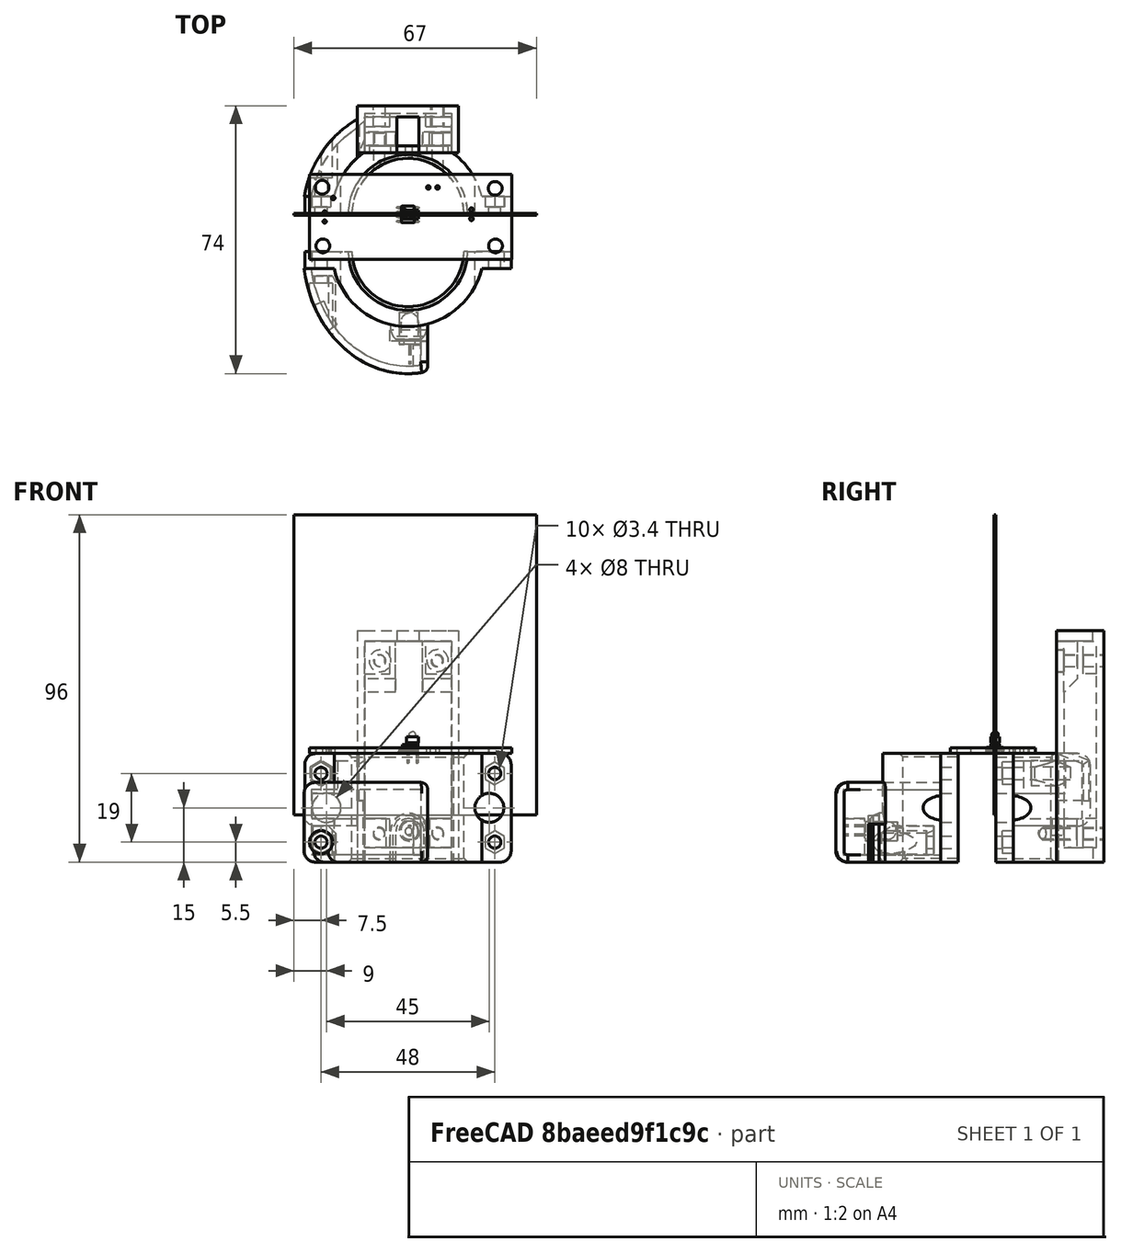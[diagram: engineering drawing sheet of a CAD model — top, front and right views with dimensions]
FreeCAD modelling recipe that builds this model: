
FCSTD DOCUMENT  (FreeCAD 0.21R33668 +26 (Git))
Label: Senzor
License: All rights reserved
LicenseURL: http://en.wikipedia.org/wiki/All_rights_reserved
objects: Part::Box×33, Part::Cut×27, Part::Cylinder×24, Part::MultiFuse×22, App::Part×20, Part::Feature×19, Part::Chamfer×17, Part::Prism×5, Part::Fillet×5, Part::FeaturePython×4, Part::Part2DObjectPython×4, Part::Extrusion×4, Part::MultiCommon×2, Part::Thickness×2, Part::Wedge×1, Spreadsheet::Sheet×1, App::DocumentObjectGroup×1
note: 169 computed .brp shape members not serialized (recipe doc carries the construction recipe); baked Part::Feature solids carry a one-line shape summary decoded from their .brp

FEATURE [Part::Box] Box022  label="Cube022"
  AttacherType = Attacher::AttachEngine3D
  Height = 4
  Length = 24
  Placement = pos=(-12,16,26) rot=(0,0,1;0rad)
  Width = 11
FEATURE [Part::Cylinder] Cylinder017
  Angle = 360
  AttacherType = Attacher::AttachEngine3D
  FirstAngle = 0
  Height = 30
  Radius = 15.5
  SecondAngle = 0
FEATURE [Part::Cylinder] Cylinder018
  Angle = 360
  AttacherType = Attacher::AttachEngine3D
  FirstAngle = 0
  Height = 30
  Radius = 21
  SecondAngle = 0
FEATURE [Part::Box] Box024  label="Cube024"
  AttacherType = Attacher::AttachEngine3D
  Height = 8
  Length = 24
  Placement = pos=(-12,15.5,18) rot=(0,0,1;0rad)
  Width = 7
FEATURE [Part::Box] Box025  label="Cube025"
  AttacherType = Attacher::AttachEngine3D
  Height = 8
  Length = 24
  Placement = pos=(12,27,18) rot=(0,0,1;3.14159rad)
  Width = 2.5
FEATURE [Part::Cut] Cut026
  Base = -> Cylinder018
  Tool = -> Cylinder017
FEATURE [Part::Box] Box027  label="Cube027"
  AttacherType = Attacher::AttachEngine3D
  Height = 35
  Length = 29
  Placement = pos=(-14,18,-17) rot=(0,0,1;0rad)
  Width = 11
FEATURE [Part::Cut] Cut027
  Base = -> Cut026
  Tool = -> Box027
FEATURE [Part::Box] Box028  label="Cube028"
  AttacherType = Attacher::AttachEngine3D
  Height = 20
  Length = 12
  Placement = pos=(-6,19,6) rot=(0,0,1;0rad)
  Width = 5
FEATURE [Part::MultiFuse] Fusion015
  Shapes = -> [Cut027,Box024]
FEATURE [Part::Cut] Cut028
  Base = -> Fusion015
  Tool = -> Box028
FEATURE [Part::Cylinder] Cylinder023
  Angle = 360
  AttacherType = Attacher::AttachEngine3D
  FirstAngle = 0
  Height = 44
  Placement = pos=(-0.2,19.5,21.5) rot=(1,0,0;1.5708rad)
  Radius = 1
  SecondAngle = 0
FEATURE [Part::Cylinder] Cylinder024
  Angle = 360
  AttacherType = Attacher::AttachEngine3D
  FirstAngle = 0
  Height = 5
  Placement = pos=(-0.2,-17,21.5) rot=(1,0,0;1.5708rad)
  Radius = 2.6
  SecondAngle = 0
FEATURE [Part::Cylinder] Cylinder025
  Angle = 360
  AttacherType = Attacher::AttachEngine3D
  FirstAngle = 0
  Height = 22
  Placement = pos=(0,0,-3) rot=(0,0,1;0rad)
  Radius = 1.7
  SecondAngle = 0
FEATURE [Part::Prism] Prism003
  AttacherType = Attacher::AttachEngine3D
  Circumradius = 3.1
  FirstAngle = 0
  Height = 4
  Polygon = 6
  SecondAngle = 0
FEATURE [Part::MultiFuse] Fusion017
  Placement = pos=(24,6,5.5) rot=(0.935113,-0.250563,0.250563;1.63783rad)
  Shapes = -> [Cylinder025,Prism003]
FEATURE [Part::Box] Box031  label="Cube031"
  AttacherType = Attacher::AttachEngine3D
  Height = 19
  Length = 7.5
  Placement = pos=(-4,18,-31.5) rot=(0,0,1;0rad)
  Width = 10
FEATURE [Part::Box] Box032  label="Cube032"
  AttacherType = Attacher::AttachEngine3D
  Height = 83
  Length = 67
  Placement = pos=(-31.5,-0.25,-17) rot=(0,0,1;0rad)
  Width = 0.5
FEATURE [Part::Box] Box033  label="Cube033"
  AttacherType = Attacher::AttachEngine3D
  Height = 30
  Length = 11
  Placement = pos=(17.5,-5,0) rot=(0,0,1;0rad)
  Width = 10
FEATURE [Part::Cylinder] Cylinder032
  Angle = 360
  AttacherType = Attacher::AttachEngine3D
  FirstAngle = 0
  Height = 22
  Placement = pos=(0,0,-3) rot=(0,0,1;0rad)
  Radius = 1.7
  SecondAngle = 0
FEATURE [Part::Cylinder] Cylinder034
  Angle = 360
  AttacherType = Attacher::AttachEngine3D
  FirstAngle = 0
  Height = 32
  Placement = pos=(22.5,13,15) rot=(1,0,0;1.5708rad)
  Radius = 4
  SecondAngle = 0
FEATURE [Part::Prism] Prism006
  AttacherType = Attacher::AttachEngine3D
  Circumradius = 3.1
  FirstAngle = 0
  Height = 4
  Polygon = 6
  SecondAngle = 0
FEATURE [Part::MultiFuse] Fusion021
  Placement = pos=(24,6,24.5) rot=(0.935113,-0.250563,0.250563;1.63783rad)
  Shapes = -> [Cylinder032,Prism006]
FEATURE [Part::Chamfer] Chamfer022
  Base = -> Box022
  Edges = 1 edges r=0.6: [Edge10]
FEATURE [Part::Cylinder] Cylinder030
  Angle = 360
  AttacherType = Attacher::AttachEngine3D
  FirstAngle = 0
  Height = 17
  Placement = pos=(7.7,28,-25.6) rot=(1,0,0;1.5708rad)
  Radius = 1.6
  SecondAngle = 0
FEATURE [Part::Cylinder] Cylinder031
  Angle = 360
  AttacherType = Attacher::AttachEngine3D
  FirstAngle = 0
  Height = 15
  Placement = pos=(-8.2,27,-25.7) rot=(1,0,0;1.5708rad)
  Radius = 1.6
  SecondAngle = 0
FEATURE [Part::Box] Box026  label="Cube026"
  AttacherType = Attacher::AttachEngine3D
  Height = 49
  Length = 24
  Placement = pos=(-12,17,-31) rot=(0,0,1;0rad)
  Width = 2
FEATURE [Part::Box] Box034  label="Cube034"
  AttacherType = Attacher::AttachEngine3D
  Height = 14
  Length = 24
  Placement = pos=(-12,19,-31) rot=(0,0,1;0rad)
  Width = 3.7
FEATURE [Part::Chamfer] Chamfer023
  Base = -> Box034
  Edges = 1 edges r=3.6: [Edge12]
FEATURE [Part::Cut] Cut048
  Base = -> Chamfer023
  Tool = -> Box031
FEATURE [Part::MultiFuse] Fusion025
  Shapes = -> [Cut048,Box026]
FEATURE [Part::MultiFuse] Fusion026
  Shapes = -> [Cylinder030,Cylinder031]
FEATURE [Part::Cut] Cut049
  Base = -> Fusion025
  Tool = -> Fusion026
FEATURE [Part::Cylinder] Cylinder035
  Angle = 360
  AttacherType = Attacher::AttachEngine3D
  FirstAngle = 0
  Height = 17
  Placement = pos=(-8.2,28,22) rot=(1,0,0;1.5708rad)
  Radius = 1.6
  SecondAngle = 0
FEATURE [Part::Cylinder] Cylinder036
  Angle = 360
  AttacherType = Attacher::AttachEngine3D
  FirstAngle = 0
  Height = 17
  Placement = pos=(8,28,22.2) rot=(1,0,0;1.5708rad)
  Radius = 1.6
  SecondAngle = 0
FEATURE [Part::Cut] Cut050
  Base = -> Cut028
  Tool = -> Cylinder023
FEATURE [Part::Cut] Cut051
  Base = -> Cut050
  Tool = -> Cylinder024
FEATURE [Part::MultiFuse] Fusion027
  Shapes = -> [Cylinder036,Cylinder035]
FEATURE [Part::Cylinder] Cylinder037
  Angle = 360
  AttacherType = Attacher::AttachEngine3D
  FirstAngle = 0
  Height = 10
  Placement = pos=(-8.2,19,-25.7) rot=(1,0,0;1.5708rad)
  Radius = 3
  SecondAngle = 0
FEATURE [Part::Cylinder] Cylinder038
  Angle = 360
  AttacherType = Attacher::AttachEngine3D
  FirstAngle = 0
  Height = 10
  Placement = pos=(7.7,19,-25.6) rot=(1,0,0;1.5708rad)
  Radius = 3
  SecondAngle = 0
FEATURE [Part::MultiFuse] Fusion031
  Shapes = -> [Cylinder037,Cylinder038]
FEATURE [Part::Cut] Cut053
  Base = -> Cut049
  Tool = -> Fusion031
FEATURE [Part::Feature] Solid  label="LED_D5.0mm_Clear"
  Placement = pos=(0.5,-38.9,-20) rot=(0.57735,-0.57735,-0.57735;4.18879rad)
  shape: bbox 5.8 x 14.1 x 5.4 mm, 16 faces (baked)
FEATURE [Part::Box] Box035  label="Cube035"
  AttacherType = Attacher::AttachEngine3D
  Height = 10
  Length = 10
  Placement = pos=(-5,21.5,14) rot=(0,0,1;0rad)
  Width = 6.5
FEATURE [Part::Cut] Cut054
  Base = -> Box033
  Tool = -> Fusion021
FEATURE [Part::Cut] Cut055
  Base = -> Cut054
  Tool = -> Fusion017
FEATURE [Part::Cut] Cut056
  Base = -> Box025
  Tool = -> Box035
FEATURE [Part::Box] Box036  label="Cube036"
  AttacherType = Attacher::AttachEngine3D
  Height = 30
  Length = 11
  Placement = pos=(17.5,-5,0) rot=(0,0,1;0rad)
  Width = 10
FEATURE [Part::Cylinder] Cylinder039
  Angle = 360
  AttacherType = Attacher::AttachEngine3D
  FirstAngle = 0
  Height = 22
  Placement = pos=(0,0,-3) rot=(0,0,1;0rad)
  Radius = 1.7
  SecondAngle = 0
FEATURE [Part::Cylinder] Cylinder040
  Angle = 360
  AttacherType = Attacher::AttachEngine3D
  FirstAngle = 0
  Height = 22
  Placement = pos=(0,0,-3) rot=(0,0,1;0rad)
  Radius = 1.7
  SecondAngle = 0
FEATURE [Part::Prism] Prism007
  AttacherType = Attacher::AttachEngine3D
  Circumradius = 3.1
  FirstAngle = 0
  Height = 4
  Polygon = 6
  SecondAngle = 0
FEATURE [Part::MultiFuse] Fusion032
  Placement = pos=(24,6,5.5) rot=(0.935113,-0.250563,0.250563;1.63783rad)
  Shapes = -> [Cylinder039,Prism007]
FEATURE [Part::Prism] Prism008
  AttacherType = Attacher::AttachEngine3D
  Circumradius = 3.1
  FirstAngle = 0
  Height = 4
  Polygon = 6
  SecondAngle = 0
FEATURE [Part::MultiFuse] Fusion033
  Placement = pos=(24,6,24.5) rot=(0.935113,-0.250563,0.250563;1.63783rad)
  Shapes = -> [Cylinder040,Prism008]
FEATURE [Part::Cut] Cut057
  Base = -> Box036
  Tool = -> Fusion033
FEATURE [Part::Cut] Cut058
  Base = -> Cut057
  Placement = pos=(-4e-15,0,30) rot=(0,1,0;3.14159rad)
  Tool = -> Fusion032
FEATURE [Part::Cylinder] Cylinder041
  Angle = 360
  AttacherType = Attacher::AttachEngine3D
  FirstAngle = 0
  Height = 29
  Placement = pos=(-22.5,14,15) rot=(0,0.707107,-0.707107;3.14159rad)
  Radius = 4
  SecondAngle = 0
FEATURE [Part::MultiFuse] Fusion035
  Shapes = -> [Cylinder041,Cylinder034]
FEATURE [Part::FeaturePython] Tube  # WARN: FeaturePython — macro-defined, semantics opaque (R4)
  AttacherType = Attacher::AttachEngine3D
  Height = 4.5
  InnerRadius = 2.6
  OuterRadius = 5
  Placement = pos=(-0.2,-20,21.5) rot=(1,0,0;1.5708rad)
FEATURE [Part::Box] Box037  label="Cube037"
  AttacherType = Attacher::AttachEngine3D
  Height = 6
  Length = 8.5
  Placement = pos=(-5.2,-18.5,30) rot=(0.57735,0.57735,-0.57735;2.0944rad)
  Width = 10
FEATURE [Part::Cylinder] Cylinder042
  Angle = 360
  AttacherType = Attacher::AttachEngine3D
  FirstAngle = 0
  Height = 10
  Placement = pos=(-0.2,-18,21.5) rot=(1,0,0;1.5708rad)
  Radius = 3
  SecondAngle = 0
FEATURE [Part::Chamfer] Chamfer024
  Base = -> Tube
  Edges = 1 edges r=1.5: [Edge1]
FEATURE [Part::Cut] Cut061
  Base = -> Box037
  Tool = -> Cylinder042
FEATURE [Part::Chamfer] Chamfer025
  Base = -> Cut061
  Edges = 2 edges r=1.5: [Edge7,Edge8]
FEATURE [Part::Chamfer] Chamfer026
  Base = -> Chamfer024
  Edges = 1 edges r=1: [Edge2]
FEATURE [Part::Chamfer] Chamfer027
  Base = -> Chamfer025
  Edges = 2 edges r=1: [Edge9,Edge21]
FEATURE [Part::Box] Box038  label="Cube038"
  AttacherType = Attacher::AttachEngine3D
  Height = 61
  Length = 24
  Placement = pos=(-12,28,-30) rot=(0,0,1;0rad)
  Width = 2
FEATURE [Part::Feature] Part__Feature020  label="SOLID019"
  shape: bbox 6 x 4.9 x 1.75 mm, 156 faces (baked)
FEATURE [Part::Feature] Part__Feature021  label="SOLID020"
  shape: bbox 3.2 x 1.6 x 0.55 mm, 26 faces (baked)
FEATURE [Part::Feature] Part__Feature022  label="SOLID021"
  shape: bbox 3.2 x 1.6 x 0.55 mm, 26 faces (baked)
FEATURE [Part::Feature] Part__Feature023  label="SOLID022"
  shape: bbox 6 x 4.9 x 1.75 mm, 156 faces (baked)
FEATURE [Part::Feature] Part__Feature024  label="SOLID023"
  shape: bbox 3.2 x 1.6 x 0.55 mm, 26 faces (baked)
FEATURE [Part::Feature] Part__Feature025  label="SOLID024"
  shape: bbox 3.2 x 1.6 x 0.55 mm, 26 faces (baked)
FEATURE [Part::Feature] Part__Feature026  label="SOLID025"
  shape: bbox 3.2 x 1.6 x 0.55 mm, 26 faces (baked)
FEATURE [Part::Feature] Part__Feature027  label="SOLID026"
  shape: bbox 3.2 x 1.6 x 0.55 mm, 26 faces (baked)
FEATURE [Part::Feature] Part__Feature028  label="SOLID027"
  shape: bbox 2 x 1.25 x 1.25 mm, 28 faces (baked)
FEATURE [App::Part] C_0805_2012Metric002
  Group = -> [Part__Feature028]
  Origin = -> Origin030
  Placement = pos=(-10.508,-8.06,1.65) rot=(0,0,-1;1.5708rad)
FEATURE [Part::Feature] Part__Feature029  label="SOLID028"
  shape: bbox 3.2 x 1.6 x 0.55 mm, 26 faces (baked)
FEATURE [Part::Feature] Part__Feature030  label="SOLID029"
  shape: bbox 2 x 1.25 x 1.25 mm, 28 faces (baked)
FEATURE [App::Part] C_0805_2012Metric003
  Group = -> [Part__Feature030]
  Origin = -> Origin032
  Placement = pos=(3.97,-9.076,1.65) rot=(0,0,1;0rad)
FEATURE [Part::Feature] Part__Feature031  label="SOLID030"
  shape: bbox 3.3 x 2.4 x 8.6 mm, 19 faces (baked)
FEATURE [App::Part] LED_D1_8mm_W3_3mm_H2_4mm001  label="LED_D1.8mm_W3.3mm_H2.4mm001"
  Group = -> [Part__Feature031]
  Origin = -> Origin033
  Placement = pos=(-23,-2,2) rot=(0.707107,0.707107,0;3.14159rad)
FEATURE [Part::Feature] Part__Feature032  label="SOLID031"
  shape: bbox 3.2 x 1.6 x 0.55 mm, 26 faces (baked)
FEATURE [Part::Feature] Part__Feature033  label="SOLID032"
  shape: bbox 3.2 x 2.5 x 2.5 mm, 28 faces (baked)
FEATURE [App::Part] C_1210_3225Metric004
  Group = -> [Part__Feature033]
  Origin = -> Origin035
  Placement = pos=(5.975,2.465,1.65) rot=(0,0,1;0rad)
FEATURE [Part::Feature] Part__Feature034  label="SOLID033"
  shape: bbox 3.2 x 2.5 x 2.5 mm, 28 faces (baked)
FEATURE [App::Part] C_1210_3225Metric005
  Group = -> [Part__Feature034]
  Origin = -> Origin036
  Placement = pos=(-7.2,-0.4,1.65) rot=(0,0,1;0rad)
FEATURE [Part::Feature] Part__Feature035  label="SOLID034"
  shape: bbox 3.2 x 2.5 x 2.5 mm, 28 faces (baked)
FEATURE [App::Part] C_1210_3225Metric006
  Group = -> [Part__Feature035]
  Origin = -> Origin037
  Placement = pos=(-11,5,1.65) rot=(0,0,1;1.5708rad)
FEATURE [Part::Feature] Part__Feature036  label="SOLID035"
  shape: bbox 3.2 x 2.5 x 2.5 mm, 28 faces (baked)
FEATURE [App::Part] C_1210_3225Metric007
  Group = -> [Part__Feature036]
  Origin = -> Origin038
  Placement = pos=(-16,7,1.65) rot=(0,0,1;0rad)
FEATURE [Part::Feature] Part__Feature037  label="Sensor PCB001"
  shape: bbox 55.88 x 23.5 x 1.6 mm, 17 faces (baked)
FEATURE [App::Part] PinHeader_1x02_P2_54mm_Vertical002  label="PinHeader_1x02_P2.54mm_Vertical002"
  Origin = -> Origin021
  Placement = pos=(17.5465,1.34,1.65) rot=(0,0,1;0rad)
FEATURE [App::Part] PinHeader_1x02_P2_54mm_Vertical003  label="PinHeader_1x02_P2.54mm_Vertical003"
  Origin = -> Origin022
  Placement = pos=(8.1875,7.465,1.65) rot=(0,0,-1;1.5708rad)
FEATURE [App::Part] R_1206_3216Metric008
  Group = -> [Part__Feature021]
  Origin = -> Origin023
  Placement = pos=(-2.1,5.5,1.65) rot=(0,0,-1;1.5708rad)
FEATURE [App::Part] R_1206_3216Metric009
  Group = -> [Part__Feature022]
  Origin = -> Origin024
  Placement = pos=(12.475,2.965,1.65) rot=(0,0,1;1.5708rad)
FEATURE [App::Part] R_1206_3216Metric010
  Group = -> [Part__Feature024]
  Origin = -> Origin026
  Placement = pos=(-7.5,-7,1.65) rot=(0,0,1;1.5708rad)
FEATURE [App::Part] R_1206_3216Metric011
  Group = -> [Part__Feature025]
  Origin = -> Origin027
  Placement = pos=(8.475,-6.535,1.65) rot=(0,0,1;1.5708rad)
FEATURE [App::Part] R_1206_3216Metric012
  Group = -> [Part__Feature026]
  Origin = -> Origin028
  Placement = pos=(-16,3.5,1.65) rot=(0,0,1;3.14159rad)
FEATURE [App::Part] R_1206_3216Metric013
  Group = -> [Part__Feature027]
  Origin = -> Origin029
  Placement = pos=(12.475,-3.535,1.65) rot=(0,0,-1;1.5708rad)
FEATURE [App::Part] R_1206_3216Metric014
  Group = -> [Part__Feature029]
  Origin = -> Origin031
  Placement = pos=(-5.6,5.4,1.65) rot=(0,0,1;1.5708rad)
FEATURE [App::Part] R_1206_3216Metric015
  Group = -> [Part__Feature032]
  Origin = -> Origin034
  Placement = pos=(-16,-8,1.65) rot=(0,0,1;0rad)
FEATURE [App::Part] SOIC_8_3_9x4_9mm_P1_27mm002  label="SOIC-8_3.9x4.9mm_P1.27mm002"
  Group = -> [Part__Feature020]
  Origin = -> Origin020
  Placement = pos=(2.446,-2.98,1.65) rot=(0,0,1;0rad)
FEATURE [App::Part] SOIC_8_3_9x4_9mm_P1_27mm003  label="SOIC-8_3.9x4.9mm_P1.27mm003"
  Group = -> [Part__Feature023]
  Origin = -> Origin025
  Placement = pos=(-15.5,-2.98,1.65) rot=(0,0,1;0rad)
FEATURE [App::Part] Sensor_002  label="Sensor 002"
  Group = -> [SOIC_8_3_9x4_9mm_P1_27mm002,PinHeader_1x02_P2_54mm_Vertical002,PinHeader_1x02_P2_54mm_Vertical003,R_1206_3216Metric008,R_1206_3216Metric009,SOIC_8_3_9x4_9mm_P1_27mm003,R_1206_3216Metric010,R_1206_3216Metric011,R_1206_3216Metric012,R_1206_3216Metric013,C_0805_2012Metric002,R_1206_3216Metric014,C_0805_2012Metric003,LED_D1_8mm_W3_3mm_H2_4mm001,R_1206_3216Metric015,C_1210_3225Metric004,+4 more]
  Origin = -> Origin039
  Placement = pos=(0.8,22.7,1.5) rot=(-0.57735,-0.57735,-0.57735;2.0944rad)
FEATURE [Part::Box] Box039  label="Cube039"
  AttacherType = Attacher::AttachEngine3D
  Height = 13
  Length = 24
  Placement = pos=(-12,30,31) rot=(1,0,0;1.5708rad)
  Width = 3
FEATURE [Part::Box] Box040  label="Cube040"
  AttacherType = Attacher::AttachEngine3D
  Height = 11
  Length = 6
  Placement = pos=(3,27,28.5) rot=(0,0,1;3.14159rad)
  Width = 12
FEATURE [Part::Box] Box041  label="Cube041"
  AttacherType = Attacher::AttachEngine3D
  Height = 2
  Length = 13
  Placement = pos=(12,30,0) rot=(0.57735,-0.57735,0.57735;4.18879rad)
  Width = 30
FEATURE [Part::Box] Box042  label="Cube042"
  AttacherType = Attacher::AttachEngine3D
  Height = 2
  Length = 13
  Placement = pos=(12,30,34) rot=(0.57735,-0.57735,0.57735;4.18879rad)
  Width = 34
FEATURE [Part::Cylinder] Cylinder043
  Angle = 360
  AttacherType = Attacher::AttachEngine3D
  FirstAngle = 0
  Height = 21
  Placement = pos=(8,32,25.6) rot=(1,0,0;1.5708rad)
  Radius = 1.6
  SecondAngle = 0
FEATURE [Part::Cylinder] Cylinder044
  Angle = 360
  AttacherType = Attacher::AttachEngine3D
  FirstAngle = 0
  Height = 21
  Placement = pos=(-7.9,32,25.7) rot=(1,0,0;1.5708rad)
  Radius = 1.6
  SecondAngle = 0
FEATURE [Part::Cylinder] Cylinder045
  Angle = 360
  AttacherType = Attacher::AttachEngine3D
  FirstAngle = 0
  Height = 21
  Placement = pos=(8.3,32,-22.2) rot=(1,0,0;1.5708rad)
  Radius = 1.6
  SecondAngle = 0
FEATURE [Part::Cylinder] Cylinder046
  Angle = 360
  AttacherType = Attacher::AttachEngine3D
  FirstAngle = 0
  Height = 21
  Placement = pos=(-7.9,32,-22) rot=(1,0,0;1.5708rad)
  Radius = 1.6
  SecondAngle = 0
FEATURE [Part::Box] Box043  label="Cube043"
  AttacherType = Attacher::AttachEngine3D
  Height = 2
  Length = 13
  Placement = pos=(-14,30,34) rot=(0.57735,-0.57735,0.57735;4.18879rad)
  Width = 34
FEATURE [Part::Box] Box044  label="Cube044"
  AttacherType = Attacher::AttachEngine3D
  Height = 2
  Length = 13
  Placement = pos=(-14,30,0) rot=(0.57735,-0.57735,0.57735;4.18879rad)
  Width = 30
FEATURE [Part::Chamfer] Chamfer030
  Base = -> Box041
  Edges = 1 edges r=0.5: [Edge8]
FEATURE [Part::Chamfer] Chamfer031
  Base = -> Box044
  Edges = 1 edges r=0.5: [Edge6]
FEATURE [Part::Cut] Cut062
  Base = -> Box039
  Tool = -> Box040
FEATURE [Part::Wedge] Wedge
  AttacherType = Attacher::AttachEngine3D
  Placement = pos=(-19,17,-11) rot=(0,0,1;0rad)
  X2max = 10
  X2min = 0
  Xmax = 10
  Xmin = 0
  Ymax = 7.5
  Ymin = 0
  Z2max = 8
  Z2min = -2
  Zmax = 11
  Zmin = -2
FEATURE [Part::Cut] Cut063
  Base = -> Chamfer031
  Tool = -> Wedge
FEATURE [Part::Chamfer] Chamfer032
  Base = -> Cut063
  Edges = 2 edges r=1.5: [Edge18,Edge19]
FEATURE [Part::Box] Box045  label="Cube045"
  AttacherType = Attacher::AttachEngine3D
  Height = 8
  Length = 3.7
  Placement = pos=(-12,28,-26) rot=(0,0,-1;1.5708rad)
  Width = 24
FEATURE [Part::MultiFuse] Fusion037
  Shapes = -> [Cylinder044,Cylinder043,Cylinder045,Cylinder046]
FEATURE [Part::Box] Box046  label="Cube046"
  AttacherType = Attacher::AttachEngine3D
  Height = 10
  Length = 10
  Placement = pos=(-5,18,-28) rot=(0,0,1;0rad)
  Width = 10
FEATURE [Part::Cut] Cut065
  Base = -> Box045
  Tool = -> Box046
FEATURE [Part::MultiFuse] Fusion038
  Shapes = -> [Cut065,Box038]
FEATURE [Part::Box] Box047  label="Cube047"
  AttacherType = Attacher::AttachEngine3D
  Height = 56
  Length = 36
  Placement = pos=(5.5,-15,-43) rot=(0,0,1;3.14159rad)
  Width = 36
FEATURE [Spreadsheet::Sheet] Spreadsheet  label="Elipse"
  cells = A1='outer width; B1=25; A2='outer height; B2=30; A3='inner width; B3=10; A4='inner height; B4=21
FEATURE [Part::Part2DObjectPython] Ellipse  # Draft 2D object (typed FeaturePython)
  Area = 1385.44
  FirstAngle = 0
  LastAngle = 0
  MajorRadius = 21
  MakeFace = true
  MinorRadius = 21
  Placement = pos=(0,-10,0) rot=(0,0,-1;1.5708rad)
FEATURE [Part::Part2DObjectPython] Ellipse001  # Draft 2D object (typed FeaturePython)
  Area = 3097.61
  FirstAngle = 0
  LastAngle = 0
  MajorRadius = 34
  MakeFace = true
  MinorRadius = 29
  Placement = pos=(0,-10,0) rot=(0,0,-1;1.5708rad)
FEATURE [Part::Extrusion] Extrude
  Base = -> Ellipse
  Dir = (-5.58797e-09,-1.15412e-07,1)
  DirMode = 2
  FaceMakerClass = Part::FaceMakerBullseye
  LengthFwd = 30
  LengthRev = 0
  Placement = pos=(0,0,0) rot=(0,0,1;3.14159rad)
  Solid = false
  Symmetric = false
FEATURE [Part::Extrusion] Extrude001
  Base = -> Ellipse001
  Dir = (-5.58797e-09,-1.15412e-07,1)
  DirMode = 2
  FaceMakerClass = Part::FaceMakerBullseye
  LengthFwd = 22
  LengthRev = 0
  Placement = pos=(0,0,0) rot=(0,0,1;3.14159rad)
  Solid = false
  Symmetric = false
FEATURE [Part::Cut] Cut067
  Base = -> Extrude001
  Placement = pos=(0,-20,-30) rot=(0,0,1;0rad)
  Tool = -> Extrude
FEATURE [Part::MultiCommon] Common
  Shapes = -> [Cut067,Box047]
FEATURE [Part::Thickness] Thickness
  Faces = -> Common [Face5,Face6]
  Intersection = false
  Join = 2
  Mode = 0
  SelfIntersection = false
  Value = -2
FEATURE [Part::Cylinder] Cylinder047
  Angle = 360
  AttacherType = Attacher::AttachEngine3D
  FirstAngle = 0
  Height = 18
  Radius = 1.7
  SecondAngle = 0
FEATURE [Part::Cylinder] Cylinder048
  Angle = 360
  AttacherType = Attacher::AttachEngine3D
  FirstAngle = 0
  Height = 21
  Placement = pos=(0,0,17) rot=(0,0,1;0rad)
  Radius = 3.2
  SecondAngle = 0
FEATURE [Part::MultiFuse] Fusion040
  Placement = pos=(-24,-2,-24.5) rot=(1,0,0;1.5708rad)
  Shapes = -> [Cylinder048,Cylinder047]
FEATURE [Part::Box] Box048  label="Cube048"
  AttacherType = Attacher::AttachEngine3D
  Height = 9
  Length = 15
  Placement = pos=(-27,-17,-29) rot=(0,0,-1;1.5708rad)
  Width = 7
FEATURE [Part::Chamfer] Chamfer033
  Base = -> Box048
  Edges = 1 edges: [Edge5 r1=6 r2=12]
FEATURE [Part::Chamfer] Chamfer034
  Base = -> Chamfer033
  Edges = 1 edges: [Edge12 r1=1.8 r2=0.8]
FEATURE [Part::MultiFuse] Fusion041
  Shapes = -> [Thickness,Chamfer034]
FEATURE [Part::Cut] Cut068
  Base = -> Fusion041
  Tool = -> Fusion040
FEATURE [Part::Box] Box049  label="Cube049"
  AttacherType = Attacher::AttachEngine3D
  Height = 5
  Length = 8
  Placement = pos=(-5,-35,-32.5) rot=(0,0,1;0rad)
  Width = 6
FEATURE [Part::Box] Box050  label="Cube050"
  AttacherType = Attacher::AttachEngine3D
  Height = 13
  Length = 5
  Placement = pos=(3,-35,-32.5) rot=(0,0,1;0rad)
  Width = 6
FEATURE [Part::MultiFuse] Fusion042
  Shapes = -> [Box049,Box050]
FEATURE [Part::Cut] Cut069
  Base = -> Cut068
  Tool = -> Fusion042
FEATURE [Part::Chamfer] Chamfer035
  Base = -> Cut069
  Edges = 1 edges: [Edge50 r1=1.9 r2=2.4]
FEATURE [Part::Chamfer] Chamfer036
  Base = -> Chamfer035
  Edges = 1 edges r=2: [Edge53]
FEATURE [Part::Fillet] Fillet004
  Base = -> Chamfer036
  Edges = 2 edges r=3: [Edge56,Edge57]
FEATURE [Part::Fillet] Fillet005
  Base = -> Fillet004
  Edges = 5 edges r=2: [Edge12,Edge15,Edge21,Edge40,Edge56]
FEATURE [Part::Box] Box051  label="Cube051"
  AttacherType = Attacher::AttachEngine3D
  Height = 4
  Length = 24
  Placement = pos=(-12,27,-30) rot=(0,0,1;0rad)
  Width = 1
FEATURE [Part::Box] Box052  label="Cube052"
  AttacherType = Attacher::AttachEngine3D
  Height = 9
  Length = 3.7
  Placement = pos=(-12,28,-26) rot=(0,0,-1;1.5708rad)
  Width = 24
FEATURE [Part::Box] Box053  label="Cube053"
  AttacherType = Attacher::AttachEngine3D
  Height = 11
  Length = 10
  Placement = pos=(-5,18,-28) rot=(0,0,1;0rad)
  Width = 10
FEATURE [Part::Cut] Cut070
  Base = -> Box052
  Placement = pos=(0,0,48) rot=(0,0,1;0rad)
  Tool = -> Box053
FEATURE [Part::MultiFuse] Fusion043
  Shapes = -> [Fusion038,Cut070]
FEATURE [Part::Cut] Cut071
  Base = -> Fusion043
  Tool = -> Fusion037
FEATURE [Part::MultiFuse] Fusion044  label="Senzor_kryt_DPS"
  Shapes = -> [Cut071,Box043,Chamfer032,Box042,Chamfer030,Cut062,Box051]
FEATURE [Part::Box] Box054  label="Krychle"
  AttacherType = Attacher::AttachEngine3D
  Height = 10
  Length = 3
  Placement = pos=(1.5,-43,-28) rot=(0,0,1;0rad)
  Width = 7
FEATURE [Part::MultiFuse] Fusion045  label="Senzor_kryt_Top"
  Shapes = -> [Box054,Fillet005]
FEATURE [Part::Box] Box055  label="Cube054"
  AttacherType = Attacher::AttachEngine3D
  Height = 56
  Length = 36
  Placement = pos=(-14,41,-43) rot=(0,0,1;3.14159rad)
  Width = 36
FEATURE [Part::Part2DObjectPython] Ellipse002  # Draft 2D object (typed FeaturePython)
  Area = 1385.44
  FirstAngle = 0
  LastAngle = 0
  MajorRadius = 21
  MakeFace = true
  MinorRadius = 21
  Placement = pos=(0,-10,0) rot=(0,0,-1;1.5708rad)
FEATURE [Part::Part2DObjectPython] Ellipse003  # Draft 2D object (typed FeaturePython)
  Area = 2733.19
  FirstAngle = 0
  LastAngle = 0
  MajorRadius = 30
  MakeFace = true
  MinorRadius = 29
  Placement = pos=(0,-10,0) rot=(0,0,-1;1.5708rad)
FEATURE [Part::Extrusion] Extrude002
  Base = -> Ellipse002
  Dir = (-5.58797e-09,-1.15412e-07,1)
  DirMode = 2
  FaceMakerClass = Part::FaceMakerBullseye
  LengthFwd = 30
  LengthRev = 0
  Placement = pos=(0,0,0) rot=(0,0,1;3.14159rad)
  Solid = false
  Symmetric = false
FEATURE [Part::Extrusion] Extrude003
  Base = -> Ellipse003
  Dir = (-5.58797e-09,-1.15412e-07,1)
  DirMode = 2
  FaceMakerClass = Part::FaceMakerBullseye
  LengthFwd = 20
  LengthRev = 0
  Placement = pos=(0,0,0) rot=(0,0,1;3.14159rad)
  Solid = false
  Symmetric = false
FEATURE [Part::Cut] Cut072
  Base = -> Extrude003
  Placement = pos=(0,-10,-20) rot=(0,0,1;0rad)
  Tool = -> Extrude002
FEATURE [Part::MultiCommon] Common001
  Shapes = -> [Box055,Cut072]
FEATURE [Part::Thickness] Thickness001
  Faces = -> Common001 [Face1,Face3,Face6]
  Intersection = false
  Join = 2
  Mode = 0
  SelfIntersection = false
  Value = -2
FEATURE [Part::Fillet] Fillet006
  Base = -> Thickness001
  Edges = 2 edges r=3: [Edge4,Edge6]
FEATURE [Part::Prism] Prism001  label="3m_nut_bigger"
  AttacherType = Attacher::AttachEngine3D
  Circumradius = 3.5
  FirstAngle = 0
  Height = 12
  Placement = pos=(-24,22,-5.5) rot=(0.935113,0.250563,-0.250563;1.63783rad)
  Polygon = 6
  SecondAngle = 0
FEATURE [Part::Box] Box056  label="Cube055"
  AttacherType = Attacher::AttachEngine3D
  Height = 9
  Length = 8
  Placement = pos=(-19.5,5,-2) rot=(0,1,0;3.14159rad)
  Width = 15
FEATURE [Part::Cylinder] Cylinder049
  Angle = 360
  AttacherType = Attacher::AttachEngine3D
  FirstAngle = 0
  Height = 22
  Placement = pos=(-24,21.5,-5.5) rot=(1,0,0;1.5708rad)
  Radius = 1.7
  SecondAngle = 0
FEATURE [Part::Chamfer] Chamfer037
  Base = -> Box056
  Edges = 1 edges: [Edge7 r1=12 r2=6.5]
FEATURE [Part::Chamfer] Chamfer038
  Base = -> Chamfer037
  Edges = 1 edges: [Edge12 r1=0.9 r2=2.8]
FEATURE [Part::MultiFuse] Fusion047
  Shapes = -> [Chamfer038,Fillet006]
FEATURE [Part::MultiFuse] Fusion048
  Shapes = -> [Prism001,Cylinder049]
FEATURE [Part::Cut] Cut073  label="Senzor_kryt_Bot"
  Base = -> Fusion047
  Tool = -> Fusion048
FEATURE [Part::Fillet] Fillet002
  Base = -> Cut056
  Edges = 2 edges r=4: [Edge21,Edge22]
FEATURE [Part::MultiFuse] Fusion034
  Shapes = -> [Fillet002,Chamfer022,Cut051,Cut058,Cut055,Cut053]
FEATURE [Part::Cut] Cut059
  Base = -> Fusion034
  Tool = -> Fusion035
FEATURE [Part::Cut] Cut060
  Base = -> Cut059
  Tool = -> Fusion027
FEATURE [Part::Chamfer] Chamfer028
  Base = -> Cut060
  Edges = 1 edges r=1: [Edge114]
FEATURE [Part::Chamfer] Chamfer029
  Base = -> Chamfer028
  Edges = 1 edges r=1: [Edge43]
FEATURE [Part::MultiFuse] Fusion036
  Shapes = -> [Chamfer027,Chamfer026,Chamfer029]
FEATURE [Part::Fillet] Fillet003
  Base = -> Fusion036
  Edges = 4 edges r=3: [Edge70,Edge103,Edge172,Edge173]
FEATURE [Part::FeaturePython] Slice  # WARN: FeaturePython — macro-defined, semantics opaque (R4)
  Base = -> Fillet003
  Mode = 1
  Tolerance = 0
  Tools = -> [Box032]
FEATURE [Part::FeaturePython] Slice_child0  label="Slice.0"  # WARN: FeaturePython — macro-defined, semantics opaque (R4)
  Base = -> Slice
  FilterType = 1
  Invert = false
  OverrideMaxVal = 0
  Placement = pos=(0,0,0) rot=(0,1,0;3.14159rad)
  WindowFrom = 80
  WindowTo = 100
  items = 0
FEATURE [Part::FeaturePython] Slice_child2  label="Senzor_Top"  # WARN: FeaturePython — macro-defined, semantics opaque (R4)
  Base = -> Slice
  FilterType = 1
  Invert = false
  OverrideMaxVal = 0
  Placement = pos=(0,-10,0) rot=(0,1,0;3.14159rad)
  WindowFrom = 80
  WindowTo = 100
  items = 2
FEATURE [Part::Box] Box057  label="Cube056"
  AttacherType = Attacher::AttachEngine3D
  Height = 10
  Length = 31
  Placement = pos=(-13.5,23.5,-26) rot=(0,0,1;0rad)
  Width = 10
FEATURE [Part::Cut] Cut074  label="Senzor_Bot"
  Base = -> Slice_child0
  Tool = -> Box057
FEATURE [App::DocumentObjectGroup] GrExplode_Slice  label="Exploded Slice"
  Group = -> [Slice_child2,Cut074]
